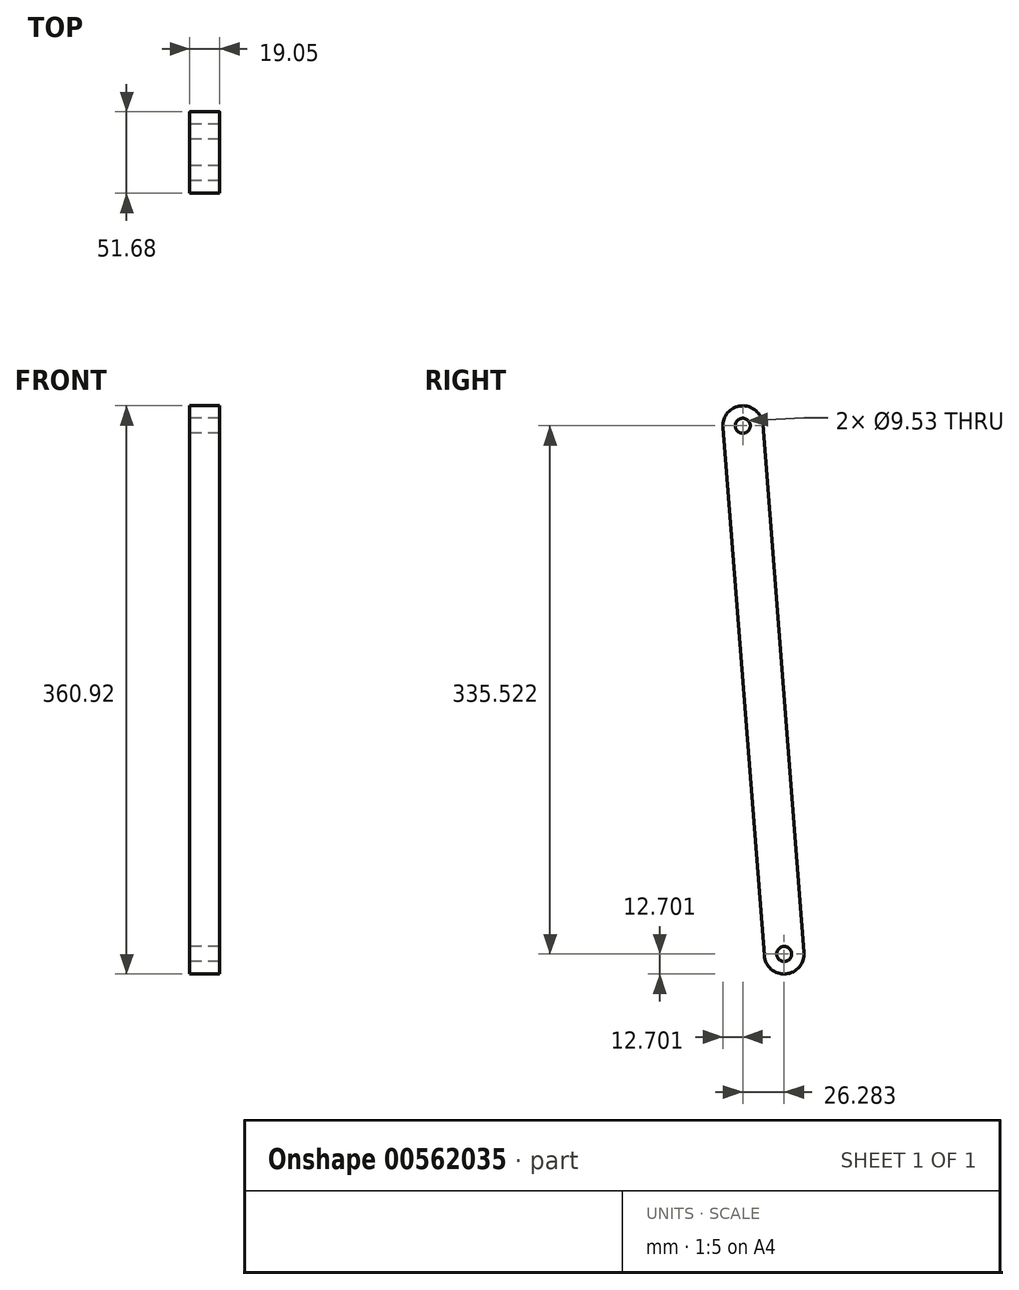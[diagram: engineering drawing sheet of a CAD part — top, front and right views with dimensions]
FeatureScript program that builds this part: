
annotation { "Feature Type Name" : "Feature", "Feature Type Description" : "" }
export const myFeature = defineFeature(function(context is Context, id is Id, definition is map)
    precondition{}
    {
        {
            var Q0;
            Q0=qCreatedBy(makeId("Right.planeOp"),FACE);
            var sketch = newSketch(context, id + "F0", { "sketchPlane" : qUnion([Q0])});
            skLineSegment(sketch, "E0", {"start": v(-513.86, 319.86) * mm, "end": v(-513.86, 78.56) * mm});
            skSolve(sketch);
        }
        {
            var Q0;
            Q0=qCreatedBy(makeId("Right.planeOp"),FACE);
            var sketch = newSketch(context, id + "F1", { "sketchPlane" : qUnion([Q0])});
            skLineSegment(sketch, "E1", {"start": v(-749.75, 255.82) * mm, "end": v(-601.81, 261.03) * mm});
            skLineSegment(sketch, "E2", {"start": v(-562.01, 653.81) * mm, "end": v(-601.81, 261.03) * mm});
            skLineSegment(sketch, "E3", {"start": v(-562.01, 653.81) * mm, "end": v(-749.75, 255.82) * mm});
            skLineSegment(sketch, "E4", {"start": v(-712.77, 291.22) * mm, "end": v(-724.6, 436.35) * mm});
            skLineSegment(sketch, "E5", {"start": v(-712.77, 291.22) * mm, "end": v(-827.72, 541.93) * mm});
            skLineSegment(sketch, "E6", {"start": v(-724.6, 436.35) * mm, "end": v(-827.72, 541.93) * mm});
            skLineSegment(sketch, "E7", {"start": v(-1010.22, 658.42) * mm, "end": v(-827.72, 541.93) * mm});
            skLineSegment(sketch, "E8", {"start": v(-1039.51, 675.34) * mm, "end": v(-1010.22, 658.42) * mm});
            skLineSegment(sketch, "E9", {"start": v(-1039.51, 675.34) * mm, "end": v(-712.77, 291.22) * mm});
            skLineSegment(sketch, "E10", {"start": v(-1010.22, 658.42) * mm, "end": v(-712.77, 291.22) * mm});
            skLineSegment(sketch, "E11", {"start": v(-601.81, 261.03) * mm, "end": v(-595.89, 401.8) * mm});
            skLineSegment(sketch, "E12", {"start": v(-601.81, 261.03) * mm, "end": v(-609.7, 655.84) * mm});
            skLineSegment(sketch, "E13", {"start": v(-595.89, 401.8) * mm, "end": v(-609.7, 655.84) * mm});
            skLineSegment(sketch, "E14", {"start": v(-724.6, 436.35) * mm, "end": v(-595.89, 401.8) * mm});
            skLineSegment(sketch, "E15", {"start": v(-827.72, 541.93) * mm, "end": v(-776.2, 589.57) * mm});
            skLineSegment(sketch, "E16", {"start": v(-749.75, 255.82) * mm, "end": v(-776.2, 589.57) * mm});
            skLineSegment(sketch, "E17", {"start": v(-1043.9, 791.38) * mm, "end": v(-776.2, 589.57) * mm});
            skLineSegment(sketch, "E18", {"start": v(-1392.46, 315.43) * mm, "end": v(-1338.48, 358.4) * mm});
            skLineSegment(sketch, "E19", {"start": v(-1338.48, 358.4) * mm, "end": v(-1296.78, 299.05) * mm});
            skLineSegment(sketch, "E20", {"start": v(-1043.9, 791.38) * mm, "end": v(-1296.78, 299.05) * mm});
            skLineSegment(sketch, "E21", {"start": v(-1296.78, 299.05) * mm, "end": v(-1039.51, 675.34) * mm});
            skLineSegment(sketch, "E22", {"start": v(-1039.51, 675.34) * mm, "end": v(-1043.9, 791.38) * mm});
            skLineSegment(sketch, "E23", {"start": v(-1010.22, 658.42) * mm, "end": v(-1338.48, 358.4) * mm});
            skLineSegment(sketch, "E24", {"start": v(-1392.46, 315.43) * mm, "end": v(-1296.78, 299.05) * mm});
            skLineSegment(sketch, "E25", {"start": v(-1296.78, 299.05) * mm, "end": v(-1296.78, 190.05) * mm});
            skLineSegment(sketch, "E26", {"start": v(-1296.78, 190.05) * mm, "end": v(-1404.89, 208.55) * mm});
            skLineSegment(sketch, "E27", {"start": v(-1404.89, 208.55) * mm, "end": v(-1392.46, 315.43) * mm});
            skLineSegment(sketch, "E28", {"start": v(-1392.46, 315.43) * mm, "end": v(-1296.78, 190.05) * mm});
            skLineSegment(sketch, "E29", {"start": v(0, 0) * mm, "end": v(0, 674.17) * mm});
            skLineSegment(sketch, "E30", {"start": v(-316.61, 320.6) * mm, "end": v(-316.61, 307.94) * mm});
            skLineSegment(sketch, "E31", {"start": v(-400.45, 218.07) * mm, "end": v(-378.01, 218.07) * mm});
            skLineSegment(sketch, "E32", {"start": v(-472.6, 74.76) * mm, "end": v(-472.6, 54.94) * mm});
            skSolve(sketch);
        }
        {
            var Q0;
            Q0=qCreatedBy(makeId("Right.planeOp"),FACE);
            var sketch = newSketch(context, id + "F2", { "sketchPlane" : qUnion([Q0])});
            skArc(sketch, "E33", {"start": v(-788.7, 590.35) * mm, "mid": v(-777.02, 604) * mm, "end": v(-763.37, 592.33) * mm});
            skArc(sketch, "E34", {"start": v(-762.4, 254.83) * mm, "mid": v(-748.75, 243.16) * mm, "end": v(-737.08, 256.81) * mm});
            skLineSegment(sketch, "E35", {"start": v(-762.4, 254.83) * mm, "end": v(-788.7, 590.35) * mm});
            skLineSegment(sketch, "E36", {"start": v(-763.37, 592.33) * mm, "end": v(-737.08, 256.81) * mm});
            skCircle(sketch, "E37", {"center": v(-776.03, 591.34) * mm, "radius": 4.76 * mm});
            skCircle(sketch, "E38", {"center": v(-749.75, 255.82) * mm, "radius": 4.76 * mm});
            skSolve(sketch);
        }
        {
            var Q0;
            Q0 = qSketchRegion(id + "F2", true);
            extrude(context, id + "F3", {"entities" : qUnion([Q0]), "depth" : 19.05 * mm, "offsetDistance" : 25.4 * mm});
        }
    });
